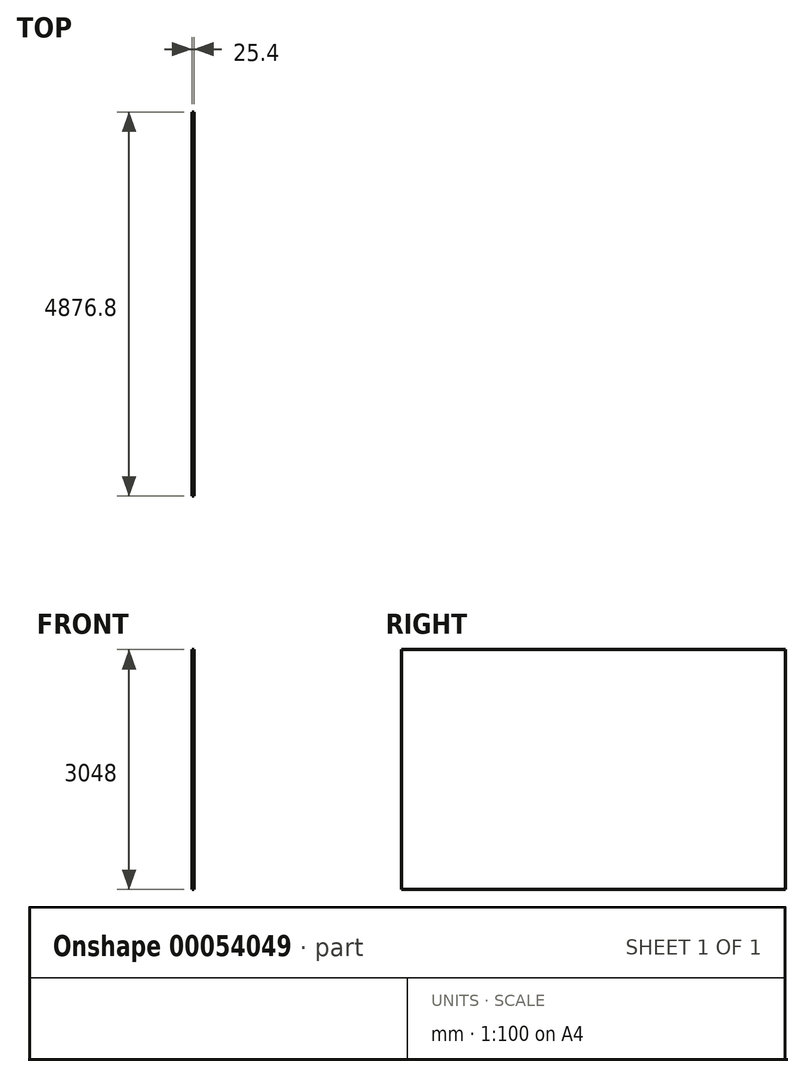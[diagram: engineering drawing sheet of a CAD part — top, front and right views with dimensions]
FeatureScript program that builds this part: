
annotation { "Feature Type Name" : "Feature", "Feature Type Description" : "" }
export const myFeature = defineFeature(function(context is Context, id is Id, definition is map)
    precondition{}
    {
        {
            var Q0;
            Q0=qCreatedBy(makeId("Right.planeOp"),FACE);
            var sketch = newSketch(context, id + "F0", { "sketchPlane" : qUnion([Q0])});
            skLineSegment(sketch, "E0.bottom", {"start": v(0, 0) * mm, "end": v(4876.8, 0) * mm});
            skLineSegment(sketch, "E0.top", {"start": v(0, 3048) * mm, "end": v(4876.8, 3048) * mm});
            skLineSegment(sketch, "E0.left", {"start": v(0, 0) * mm, "end": v(0, 3048) * mm});
            skLineSegment(sketch, "E0.right", {"start": v(4876.8, 0) * mm, "end": v(4876.8, 3048) * mm});
            skSolve(sketch);
        }
        {
            var Q0;
            Q0=makeQuery(id+"F0.imprint","IMPRINT",FACE,{"disambiguationData":[TD([[makeQuery(id+"F0.imprint","IMPRINT",EDGE,{"derivedFrom":sQuery(id+"F0.wireOp",EDGE,"E0.bottom")}),1.0]])]});
            extrude(context, id + "F1", {"entities" : qUnion([Q0]), "depth" : 25.4 * mm});
        }
    });
